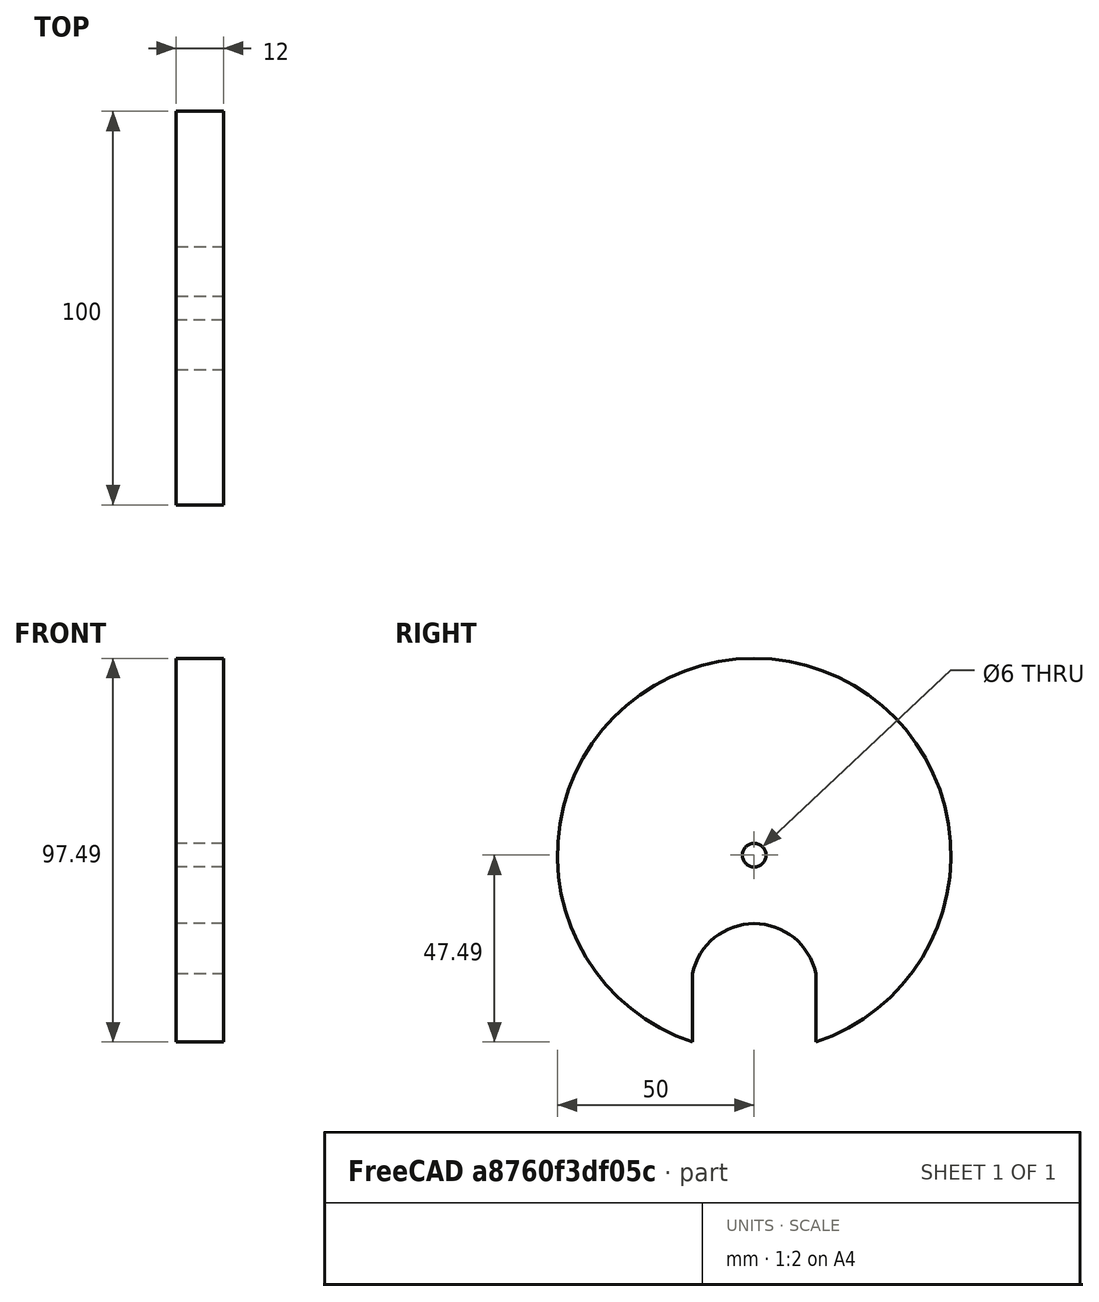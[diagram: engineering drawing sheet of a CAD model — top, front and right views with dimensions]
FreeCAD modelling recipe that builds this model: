
FCSTD DOCUMENT  (FreeCAD 0.18R16131 (Git))
Label: 300_Carosel
License: All rights reserved
LicenseURL: http://en.wikipedia.org/wiki/All_rights_reserved
objects: Sketcher::SketchObject×2, Spreadsheet::Sheet×1, App::Part×1, PartDesign::Pad×1, PartDesign::Body×1
note: 5 computed .brp shape members not serialized (recipe doc carries the construction recipe); baked Part::Feature solids carry a one-line shape summary decoded from their .brp

FEATURE [Spreadsheet::Sheet] Spreadsheet
  cells = B2=FRONT PLATE; B3=Z=; C3(T)=13; D3=.T; E3=Thichness; B4=Y=; C4(Width)=200; D4=.W; E4=Width; B5=X=; C5(Depth)=300; D5=.D; E5=Depth
FEATURE [App::Part] Part
  License = CC BY 3.0
  LicenseURL = http://creativecommons.org/licenses/by/3.0/
  Origin = -> Origin
FEATURE [Sketcher::SketchObject] Sketch
  MapMode = 5
  Placement = pos=(0,0,0) rot=(0.57735,0.57735,0.57735;2.0944rad)
  Support = -> [YZ_Plane001]
  sketch-geometry (6):
    g0: ArcOfCircle CenterX=0 CenterY=0 CenterZ=0 NormalX=0 NormalY=0 NormalZ=1 AngleXU=0 Radius=50 StartAngle=5.03067 EndAngle=10.6773
    g1: Circle CenterX=0 CenterY=0 CenterZ=0 NormalX=0 NormalY=0 NormalZ=1 AngleXU=0 Radius=3
    g2: LineSegment [constr] StartX=0 StartY=0 StartZ=0 EndX=0 EndY=-33.3981 EndZ=0
    g3: ArcOfCircle CenterX=0 CenterY=-33.3981 CenterZ=0 NormalX=0 NormalY=0 NormalZ=1 AngleXU=0 Radius=16 StartAngle=0.210586 EndAngle=2.93101
    g4: LineSegment StartX=-15.6465 StartY=-30.0536 StartZ=0 EndX=-15.6465 EndY=-47.4888 EndZ=0
    g5: LineSegment StartX=15.6465 StartY=-47.4888 StartZ=0 EndX=15.6465 EndY=-30.0536 EndZ=0
  constraints (15):
    c: Coincident(g0,g-1)
    c: Diameter(g0) = 100
    c: Coincident(g1,g0)
    c: Diameter(g1) = 6
    c: Coincident(g2,g0)
    c: Vertical(g2)
    c: Coincident(g3,g2)
    c: Diameter(g3) = 32
    c: Coincident(g4,g3)
    c: Coincident(g3,g5)
    c: Vertical(g5)
    c: Vertical(g4)
    c: Horizontal(g3,g3)
    c: Coincident(g0,g5)
    c: Coincident(g0,g4)
FEATURE [PartDesign::Pad] Pad
  Length = 12
  Length2 = 100
  Placement = pos=(0,0,0) rot=(0.57735,0.57735,0.57735;2.0944rad)
  Profile = -> Sketch
  Type = 0
FEATURE [Sketcher::SketchObject] Sketch001
  MapMode = 5
  Placement = pos=(1e-15,0,0) rot=(0.57735,0.57735,-0.57735;4.18879rad)
  sketch-geometry (3):
    g0: Circle CenterX=0 CenterY=0 CenterZ=0 NormalX=0 NormalY=0 NormalZ=1 AngleXU=0 Radius=17.5
    g1: Circle CenterX=0 CenterY=34.4245 CenterZ=0 NormalX=0 NormalY=0 NormalZ=1 AngleXU=0 Radius=15
    g2: Circle CenterX=0 CenterY=0 CenterZ=0 NormalX=0 NormalY=0 NormalZ=1 AngleXU=0 Radius=50
  constraints (6):
    c: Coincident(g0,g-1)
    c: PointOnObject(g1,g-2)
    c: Diameter(g1) = 30
    c: Diameter(g0) = 35
    c: Coincident(g2,g0)
    c: Diameter(g2) = 100
FEATURE [PartDesign::Body] Body
  Group = -> [Sketch,Pad,Sketch001]
  Origin = -> Origin001
  Tip = -> Pad
